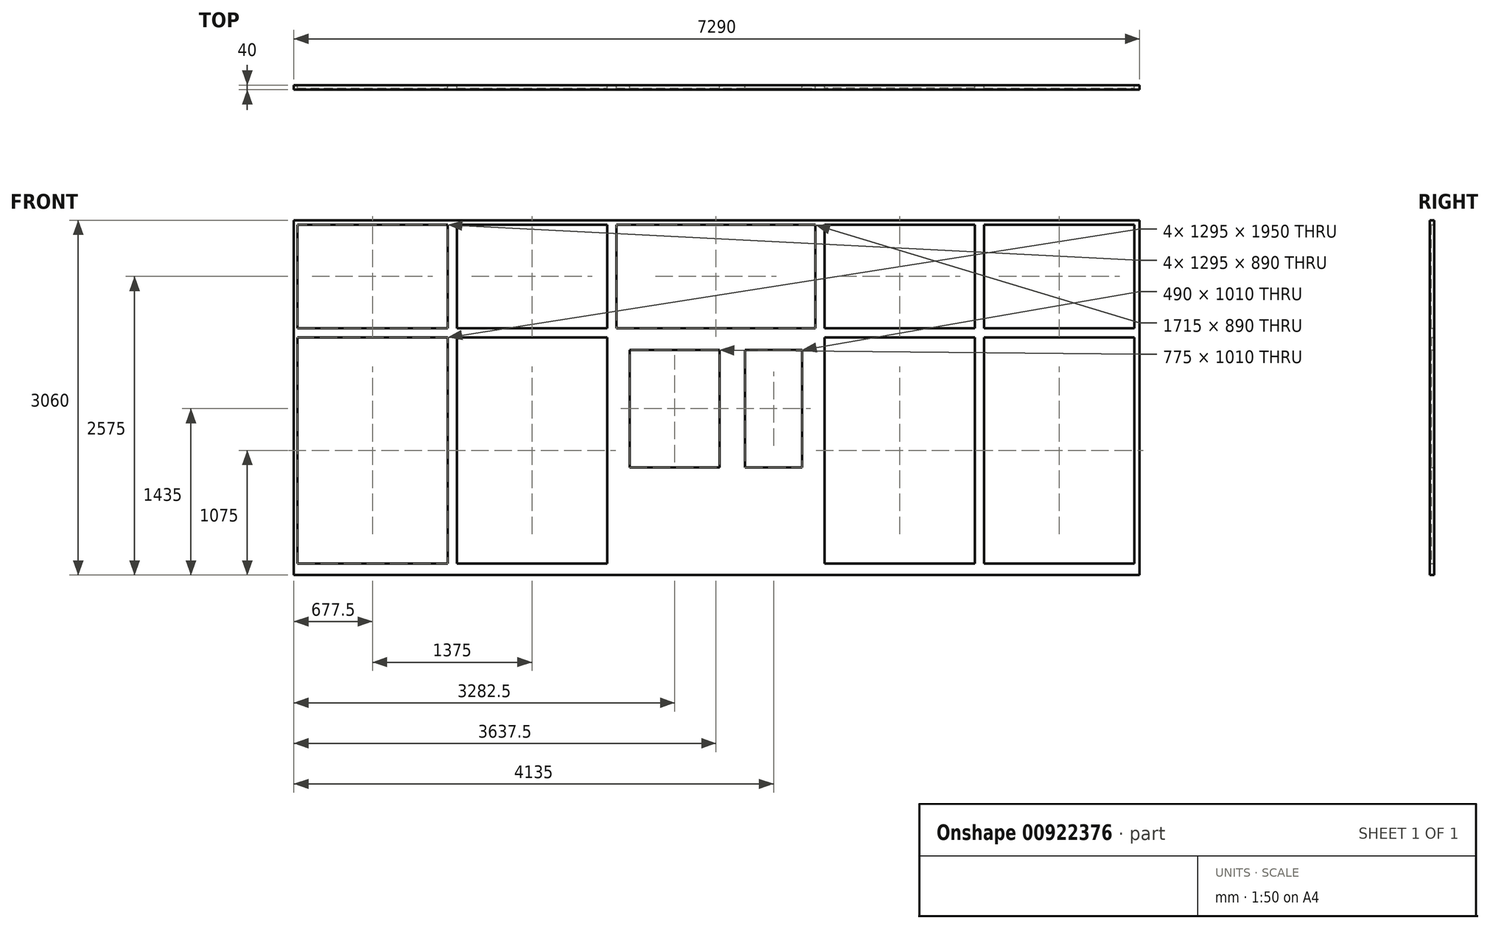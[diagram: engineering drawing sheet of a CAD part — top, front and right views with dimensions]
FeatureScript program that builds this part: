
annotation { "Feature Type Name" : "Feature", "Feature Type Description" : "" }
export const myFeature = defineFeature(function(context is Context, id is Id, definition is map)
    precondition{}
    {
        {
            var Q0;
            Q0=qCreatedBy(makeId("Front.planeOp"),FACE);
            var sketch = newSketch(context, id + "F0", { "sketchPlane" : qUnion([Q0])});
            skLineSegment(sketch, "E0", {"start": v(0, 0) * mm, "end": v(0, 100) * mm});
            skLineSegment(sketch, "E1", {"start": v(0, 100) * mm, "end": v(0, 2050) * mm});
            skLineSegment(sketch, "E2", {"start": v(0, 2050) * mm, "end": v(0, 2130) * mm});
            skLineSegment(sketch, "E3", {"start": v(0, 2130) * mm, "end": v(0, 3060) * mm});
            skLineSegment(sketch, "E4", {"start": v(0, 3060) * mm, "end": v(7290, 3060) * mm});
            skLineSegment(sketch, "E5", {"start": v(7290, 3060) * mm, "end": v(7290, 0) * mm});
            skLineSegment(sketch, "E6", {"start": v(7290, 0) * mm, "end": v(0, 0) * mm});
            skLineSegment(sketch, "E7", {"start": v(1325, 100) * mm, "end": v(1405, 100) * mm});
            skLineSegment(sketch, "E8", {"start": v(1405, 100) * mm, "end": v(2700, 100) * mm});
            skLineSegment(sketch, "E9", {"start": v(2700, 100) * mm, "end": v(2895, 100) * mm});
            skLineSegment(sketch, "E10", {"start": v(2895, 100) * mm, "end": v(3670, 100) * mm});
            skLineSegment(sketch, "E11", {"start": v(3670, 100) * mm, "end": v(3890, 100) * mm});
            skLineSegment(sketch, "E12", {"start": v(3890, 100) * mm, "end": v(4380, 100) * mm});
            skLineSegment(sketch, "E13", {"start": v(4380, 100) * mm, "end": v(4575, 100) * mm});
            skLineSegment(sketch, "E14", {"start": v(4575, 100) * mm, "end": v(5870, 100) * mm});
            skLineSegment(sketch, "E15", {"start": v(5870, 100) * mm, "end": v(5950, 100) * mm});
            skLineSegment(sketch, "E16", {"start": v(5950, 100) * mm, "end": v(7245, 100) * mm});
            skLineSegment(sketch, "E17", {"start": v(0, 100) * mm, "end": v(30, 100) * mm});
            skLineSegment(sketch, "E18", {"start": v(30, 100) * mm, "end": v(1325, 100) * mm});
            skLineSegment(sketch, "E19", {"start": v(7245, 100) * mm, "end": v(7290, 100) * mm});
            skLineSegment(sketch, "E20", {"start": v(1325, 100) * mm, "end": v(1325, 2050) * mm});
            skLineSegment(sketch, "E21", {"start": v(1325, 2050) * mm, "end": v(30, 2050) * mm});
            skLineSegment(sketch, "E22", {"start": v(30, 2050) * mm, "end": v(30, 100) * mm});
            skLineSegment(sketch, "E23", {"start": v(1405, 100) * mm, "end": v(1405, 2050) * mm});
            skLineSegment(sketch, "E24", {"start": v(1405, 2050) * mm, "end": v(2700, 2050) * mm});
            skLineSegment(sketch, "E25", {"start": v(2700, 2050) * mm, "end": v(2700, 100) * mm});
            skLineSegment(sketch, "E26", {"start": v(7245, 100) * mm, "end": v(7245, 2050) * mm});
            skLineSegment(sketch, "E27", {"start": v(7245, 2050) * mm, "end": v(5950, 2050) * mm});
            skLineSegment(sketch, "E28", {"start": v(5950, 2050) * mm, "end": v(5950, 100) * mm});
            skLineSegment(sketch, "E29", {"start": v(5870, 100) * mm, "end": v(5870, 2050) * mm});
            skLineSegment(sketch, "E30", {"start": v(5870, 2050) * mm, "end": v(4575, 2050) * mm});
            skLineSegment(sketch, "E31", {"start": v(4575, 2050) * mm, "end": v(4575, 100) * mm});
            skLineSegment(sketch, "E32", {"start": v(2895, 1940) * mm, "end": v(3670, 1940) * mm});
            skLineSegment(sketch, "E33", {"start": v(3670, 1940) * mm, "end": v(3670, 930) * mm});
            skLineSegment(sketch, "E34", {"start": v(3670, 930) * mm, "end": v(2895, 930) * mm});
            skLineSegment(sketch, "E35", {"start": v(2895, 930) * mm, "end": v(2895, 1940) * mm});
            skLineSegment(sketch, "E36", {"start": v(3890, 930) * mm, "end": v(4380, 930) * mm});
            skLineSegment(sketch, "E37", {"start": v(4380, 930) * mm, "end": v(4380, 1940) * mm});
            skLineSegment(sketch, "E38", {"start": v(4380, 1940) * mm, "end": v(3890, 1940) * mm});
            skLineSegment(sketch, "E39", {"start": v(3890, 1940) * mm, "end": v(3890, 930) * mm});
            skLineSegment(sketch, "E40", {"start": v(30, 2130) * mm, "end": v(1325, 2130) * mm});
            skLineSegment(sketch, "E41", {"start": v(1325, 2130) * mm, "end": v(1325, 3020) * mm});
            skLineSegment(sketch, "E42", {"start": v(1325, 3020) * mm, "end": v(30, 3020) * mm});
            skLineSegment(sketch, "E43", {"start": v(30, 3020) * mm, "end": v(30, 2130) * mm});
            skLineSegment(sketch, "E44", {"start": v(1405, 2130) * mm, "end": v(2700, 2130) * mm});
            skLineSegment(sketch, "E45", {"start": v(2700, 2130) * mm, "end": v(2700, 3020) * mm});
            skLineSegment(sketch, "E46", {"start": v(2700, 3020) * mm, "end": v(1405, 3020) * mm});
            skLineSegment(sketch, "E47", {"start": v(1405, 3020) * mm, "end": v(1405, 2130) * mm});
            skLineSegment(sketch, "E48", {"start": v(2780, 2130) * mm, "end": v(2780, 3020) * mm});
            skLineSegment(sketch, "E49", {"start": v(2780, 2130) * mm, "end": v(4495, 2130) * mm});
            skLineSegment(sketch, "E50", {"start": v(4495, 2130) * mm, "end": v(4495, 3020) * mm});
            skLineSegment(sketch, "E51", {"start": v(4495, 3020) * mm, "end": v(2780, 3020) * mm});
            skLineSegment(sketch, "E52", {"start": v(4575, 2130) * mm, "end": v(4575, 3020) * mm});
            skLineSegment(sketch, "E53", {"start": v(4575, 3020) * mm, "end": v(5870, 3020) * mm});
            skLineSegment(sketch, "E54", {"start": v(5870, 3020) * mm, "end": v(5870, 2130) * mm});
            skLineSegment(sketch, "E55", {"start": v(5870, 2130) * mm, "end": v(4575, 2130) * mm});
            skLineSegment(sketch, "E56", {"start": v(5950, 2130) * mm, "end": v(7245, 2130) * mm});
            skLineSegment(sketch, "E57", {"start": v(7245, 2130) * mm, "end": v(7245, 3020) * mm});
            skLineSegment(sketch, "E58", {"start": v(7245, 3020) * mm, "end": v(5950, 3020) * mm});
            skLineSegment(sketch, "E59", {"start": v(5950, 3020) * mm, "end": v(5950, 2130) * mm});
            skSolve(sketch);
        }
        {
            var Q0;
            Q0=makeQuery(id+"F0.imprint","IMPRINT",FACE,{"disambiguationData":[TD([[makeQuery(id+"F0.imprint","IMPRINT",EDGE,{"derivedFrom":sQuery(id+"F0.wireOp",EDGE,"E40")}),1.0]])]});
            var Q1;
            Q1=makeQuery(id+"F0.imprint","IMPRINT",FACE,{"disambiguationData":[TD([[makeQuery(id+"F0.imprint","IMPRINT",EDGE,{"derivedFrom":sQuery(id+"F0.wireOp",EDGE,"E18")}),1.0]])]});
            var Q2;
            Q2=makeQuery(id+"F0.imprint","IMPRINT",FACE,{"disambiguationData":[TD([[makeQuery(id+"F0.imprint","IMPRINT",EDGE,{"derivedFrom":sQuery(id+"F0.wireOp",EDGE,"E44")}),1.0]])]});
            var Q3;
            Q3=makeQuery(id+"F0.imprint","IMPRINT",FACE,{"disambiguationData":[TD([[makeQuery(id+"F0.imprint","IMPRINT",EDGE,{"derivedFrom":sQuery(id+"F0.wireOp",EDGE,"E8")}),1.0]])]});
            var Q4;
            Q4=makeQuery(id+"F0.imprint","IMPRINT",FACE,{"disambiguationData":[TD([[makeQuery(id+"F0.imprint","IMPRINT",EDGE,{"derivedFrom":sQuery(id+"F0.wireOp",EDGE,"E48")}),-1.0]])]});
            var Q5;
            Q5=makeQuery(id+"F0.imprint","IMPRINT",FACE,{"disambiguationData":[TD([[makeQuery(id+"F0.imprint","IMPRINT",EDGE,{"derivedFrom":sQuery(id+"F0.wireOp",EDGE,"E32")}),-1.0]])]});
            var Q6;
            Q6=makeQuery(id+"F0.imprint","IMPRINT",FACE,{"disambiguationData":[TD([[makeQuery(id+"F0.imprint","IMPRINT",EDGE,{"derivedFrom":sQuery(id+"F0.wireOp",EDGE,"E36")}),1.0]])]});
            var Q7;
            Q7=makeQuery(id+"F0.imprint","IMPRINT",FACE,{"disambiguationData":[TD([[makeQuery(id+"F0.imprint","IMPRINT",EDGE,{"derivedFrom":sQuery(id+"F0.wireOp",EDGE,"E52")}),-1.0]])]});
            var Q8;
            Q8=makeQuery(id+"F0.imprint","IMPRINT",FACE,{"disambiguationData":[TD([[makeQuery(id+"F0.imprint","IMPRINT",EDGE,{"derivedFrom":sQuery(id+"F0.wireOp",EDGE,"E14")}),1.0]])]});
            var Q9;
            Q9=makeQuery(id+"F0.imprint","IMPRINT",FACE,{"disambiguationData":[TD([[makeQuery(id+"F0.imprint","IMPRINT",EDGE,{"derivedFrom":sQuery(id+"F0.wireOp",EDGE,"E56")}),1.0]])]});
            var Q10;
            Q10=makeQuery(id+"F0.imprint","IMPRINT",FACE,{"disambiguationData":[TD([[makeQuery(id+"F0.imprint","IMPRINT",EDGE,{"derivedFrom":sQuery(id+"F0.wireOp",EDGE,"E16")}),1.0]])]});
            extrude(context, id + "F1", {"entities" : qUnion([Q0, Q1, Q2, Q3, Q4, Q5, Q6, Q7, Q8, Q9, Q10]), "depth" : 25 * mm, "offsetDistance" : 25 * mm});
        }
        {
            var Q0;
            Q0 = qSketchRegion(id + "F0", true);
            extrude(context, id + "F2", {"entities" : qUnion([Q0]), "depth" : 40 * mm, "offsetDistance" : 25 * mm});
        }
    });
